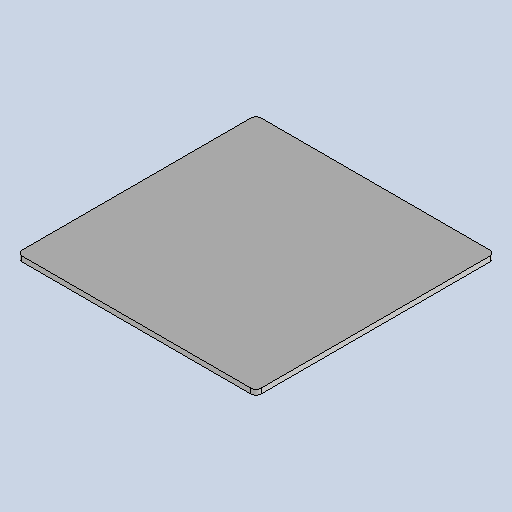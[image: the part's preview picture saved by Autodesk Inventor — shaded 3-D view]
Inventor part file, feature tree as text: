
AUTODESK INVENTOR PART (.ipt)
format: ipt  version: 2025.1 (Build 291241020, 241B)  size: 141,824 bytes
history: native  units: mm
features: other x2, sheet_metal_op x1, chamfer x1, sketch x1
ambient origin geometry x8: Origin, YZ Plane, XZ Plane, XY Plane, X Axis, Y Axis, Z Axis, Center Point
bodies: Body1 (feature_tree)
feature tree (5):
  sheet_metal_op  "Face3"
  chamfer  "Corner Round1"
  sketch  "Sketch1"  dims[d154=94.0mm d155=94.0mm d156=2.0mm d178=2.0mm]
  other  "Plate5"
  other  "Definition1"
